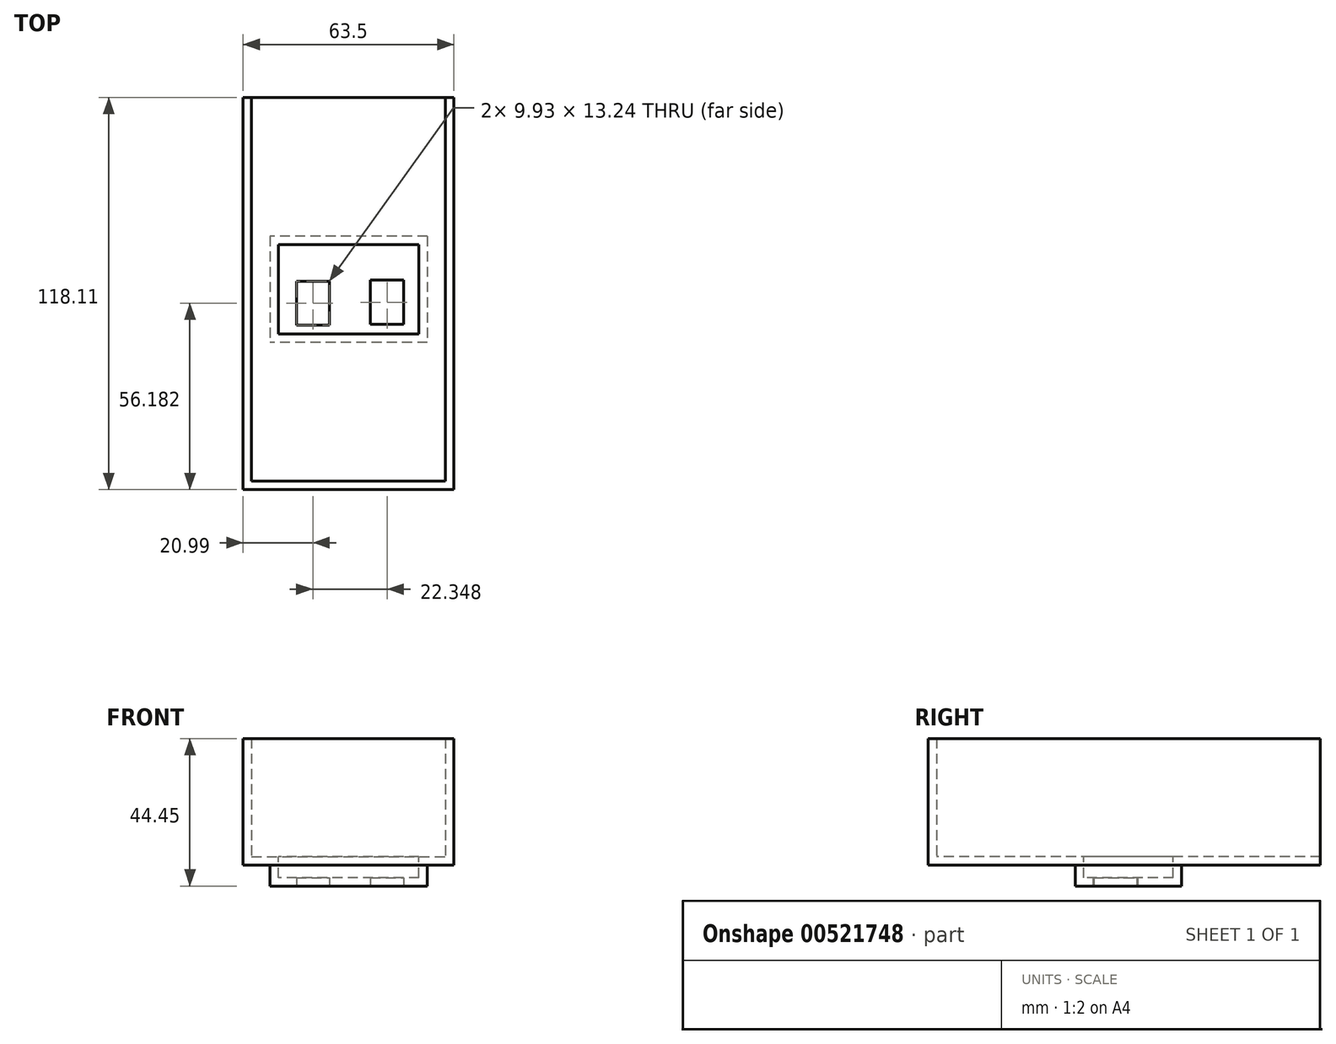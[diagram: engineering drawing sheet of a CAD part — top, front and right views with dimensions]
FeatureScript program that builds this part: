
annotation { "Feature Type Name" : "Feature", "Feature Type Description" : "" }
export const myFeature = defineFeature(function(context is Context, id is Id, definition is map)
    precondition{}
    {
        {
            var Q0;
            Q0=qCreatedBy(makeId("Top.planeOp"),FACE);
            var sketch = newSketch(context, id + "F0", { "sketchPlane" : qUnion([Q0])});
            skLineSegment(sketch, "E0.bottom", {"start": v(-31.75, 60.33) * mm, "end": v(31.75, 60.33) * mm});
            skLineSegment(sketch, "E0.top", {"start": v(-31.75, -60.32) * mm, "end": v(31.75, -60.32) * mm});
            skLineSegment(sketch, "E0.left", {"start": v(-31.75, 60.33) * mm, "end": v(-31.75, -60.32) * mm});
            skLineSegment(sketch, "E0.right", {"start": v(31.75, 60.33) * mm, "end": v(31.75, -60.32) * mm});
            skPoint(sketch, "E0.middle", {"position": v(0, 0) * mm});
            skSolve(sketch);
        }
        {
            var Q0;
            Q0=qCreatedBy(makeId("Top.planeOp"),FACE);
            var sketch = newSketch(context, id + "F1", { "sketchPlane" : qUnion([Q0])});
            skLineSegment(sketch, "E1.bottom", {"start": v(23.73, 16) * mm, "end": v(-23.73, 16) * mm});
            skLineSegment(sketch, "E1.top", {"start": v(23.73, -16) * mm, "end": v(-23.73, -16) * mm});
            skLineSegment(sketch, "E1.left", {"start": v(23.73, 16) * mm, "end": v(23.73, -16) * mm});
            skLineSegment(sketch, "E1.right", {"start": v(-23.73, 16) * mm, "end": v(-23.73, -16) * mm});
            skPoint(sketch, "E1.middle", {"position": v(0, 0) * mm});
            skSolve(sketch);
        }
        {
            var Q0;
            Q0=makeQuery(id+"F1.imprint","IMPRINT",FACE,{"disambiguationData":[TD([[makeQuery(id+"F1.imprint","IMPRINT",EDGE,{"derivedFrom":sQuery(id+"F1.wireOp",EDGE,"E1.bottom")}),1.0]])]});
            extrude(context, id + "F2", {"entities" : qUnion([Q0]), "oppositeDirection" : true, "depth" : 6.35 * mm, "offsetDistance" : 25.4 * mm});
        }
        {
            var Q0;
            Q0=makeQuery(id+"F0.imprint","IMPRINT",FACE,{"disambiguationData":[TD([[makeQuery(id+"F0.imprint","IMPRINT",EDGE,{"derivedFrom":sQuery(id+"F0.wireOp",EDGE,"E0.bottom")}),-1.0]])]});
            extrude(context, id + "F3", {"entities" : qUnion([Q0]), "operationType" : NewBodyOperationType.ADD, "depth" : 38.1 * mm, "offsetDistance" : 25.4 * mm});
        }
        {
            var Q0;
            Q0=makeQuery(id+"F3.opExtrude","CAP_FACE",FACE,{"disambiguationData":[OSD([sQuery(id+"F0.wireOp",EDGE,"E0.bottom"),sQuery(id+"F0.wireOp",EDGE,"E0.top"),sQuery(id+"F0.wireOp",EDGE,"E0.left"),sQuery(id+"F0.wireOp",EDGE,"E0.right")])],"isStart":false});
            shell(context, id + "F4", {"entities" : qUnion([Q0]), "thickness" : 2.54 * mm});
        }
        {
            var Q0;
            Q0=makeQuery(id+"F3.opExtrude","SWEPT_FACE",FACE,{"disambiguationData":[OSD([sQuery(id+"F0.wireOp",EDGE,"E0.bottom")])]});
            extrude(context, id + "F5", {"entities" : qUnion([Q0]), "operationType" : NewBodyOperationType.REMOVE, "oppositeDirection" : true, "depth" : 2.54 * mm, "offsetDistance" : 25.4 * mm});
        }
        {
            var Q0;
            Q0=makeQuery(id+"F2.opExtrude","CAP_FACE",FACE,{"disambiguationData":[OSD([sQuery(id+"F1.wireOp",EDGE,"E1.bottom"),sQuery(id+"F1.wireOp",EDGE,"E1.top"),sQuery(id+"F1.wireOp",EDGE,"E1.left"),sQuery(id+"F1.wireOp",EDGE,"E1.right")])],"isStart":false});
            var sketch = newSketch(context, id + "F6", { "sketchPlane" : qUnion([Q0])});
            skLineSegment(sketch, "E2.bottom", {"start": v(16.55, -2.76) * mm, "end": v(6.62, -2.76) * mm});
            skLineSegment(sketch, "E2.top", {"start": v(16.55, 10.48) * mm, "end": v(6.62, 10.48) * mm});
            skLineSegment(sketch, "E2.left", {"start": v(16.55, -2.76) * mm, "end": v(16.55, 10.48) * mm});
            skLineSegment(sketch, "E2.right", {"start": v(6.62, -2.76) * mm, "end": v(6.62, 10.48) * mm});
            skLineSegment(sketch, "E3.bottom", {"start": v(-5.8, -2.48) * mm, "end": v(-15.73, -2.48) * mm});
            skLineSegment(sketch, "E3.top", {"start": v(-5.8, 10.76) * mm, "end": v(-15.73, 10.76) * mm});
            skLineSegment(sketch, "E3.left", {"start": v(-5.8, -2.48) * mm, "end": v(-5.8, 10.76) * mm});
            skLineSegment(sketch, "E3.right", {"start": v(-15.73, -2.48) * mm, "end": v(-15.73, 10.76) * mm});
            skSolve(sketch);
        }
        {
            var Q0;
            Q0=makeQuery(id+"F6.imprint","IMPRINT",FACE,{"disambiguationData":[TD([[makeQuery(id+"F6.imprint","IMPRINT",EDGE,{"derivedFrom":sQuery(id+"F6.wireOp",EDGE,"E2.bottom")}),-1.0]])]});
            var Q1;
            Q1=makeQuery(id+"F6.imprint","IMPRINT",FACE,{"disambiguationData":[TD([[makeQuery(id+"F6.imprint","IMPRINT",EDGE,{"derivedFrom":sQuery(id+"F6.wireOp",EDGE,"E3.bottom")}),-1.0]])]});
            extrude(context, id + "F7", {"entities" : qUnion([Q0, Q1]), "operationType" : NewBodyOperationType.REMOVE, "endBound" : BoundingType.THROUGH_ALL, "oppositeDirection" : true, "depth" : 2.54 * mm, "offsetDistance" : 25.4 * mm});
        }
    });
